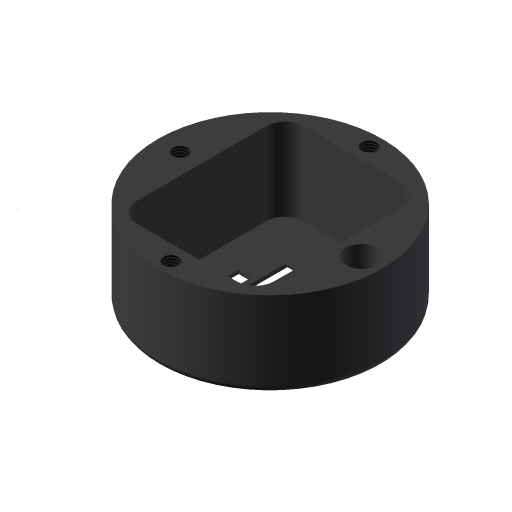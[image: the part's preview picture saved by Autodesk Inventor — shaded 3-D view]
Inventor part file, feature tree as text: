
AUTODESK INVENTOR PART (.ipt)
format: ipt  version: 2023 (Build 270158000, 158)  size: 192,000 bytes
history: native  units: mm
features: sketch x8, extrude x6, thread x3, fillet x3
ambient origin geometry x8: Origin, YZ Plane, XZ Plane, XY Plane, X Axis, Y Axis, Z Axis, Center Point
bodies: Solid1 (feature_tree)
feature tree (20):
  sketch  "Sketch1"  dims[d0=37.0mm d1=44.9mm]
  sketch  "Sketch2"  dims[d5=1.0mm d6=0.0mm d7=22.0mm d8=0.0mm]
  extrude  "Extrusion1"  Depth=44.9mm
  extrude  "Extrusion2"  Depth=1.0mm TaperAngle=0.0deg
  extrude  "Extrusion3"  Depth=22.0mm TaperAngle=0.0deg
  sketch  "Sketch4"  dims[d23=6.0mm d24=4.0mm]
  sketch  "Sketch6"  dims[d25=3.5mm d26=4.0mm d27=3.5mm d28=4.0mm d29=10.0mm d30=0.0mm d31=10.0mm d32=0.0mm d33=10.0mm d34=0.0mm]
  extrude  "Extrusion5"  Depth=4.0mm
  extrude  "Extrusion6"  Depth=10.0mm
  thread  "Thread4"  [1 undecoded]
  thread  "Thread5"  [1 undecoded]
  thread  "Thread6"  [1 undecoded]
  sketch  "Sketch8"  dims[d49=12.0mm]
  fillet  "Fillet1"  Radius=10.0mm
  fillet  "Fillet2"  Radius=10.0mm
  extrude  "Extrusion8"  Depth=5.0mm
  fillet  "Fillet3"  Radius=5.0mm
  sketch  "Sketch3"  dims[d9=8.18mm d10=22.0mm d11=0.0mm]
  sketch  "Sketch7"  dims[d35=10.0mm d36=0.0mm d37=10.0mm d38=0.0mm d45=2.0mm d46=5.0mm]
  sketch  "Sketch10"  dims[d50=20.0mm d51=3.5mm d52=5.0mm d53=3.5mm d54=5.0mm d55=2.0mm d56=0.0mm d57=1.0mm]
note: 3 required parameter values undecoded (feature->parameter linkage not recoverable at this tier; creation-order binding heuristic only, values carry confidence <= 0.55)
